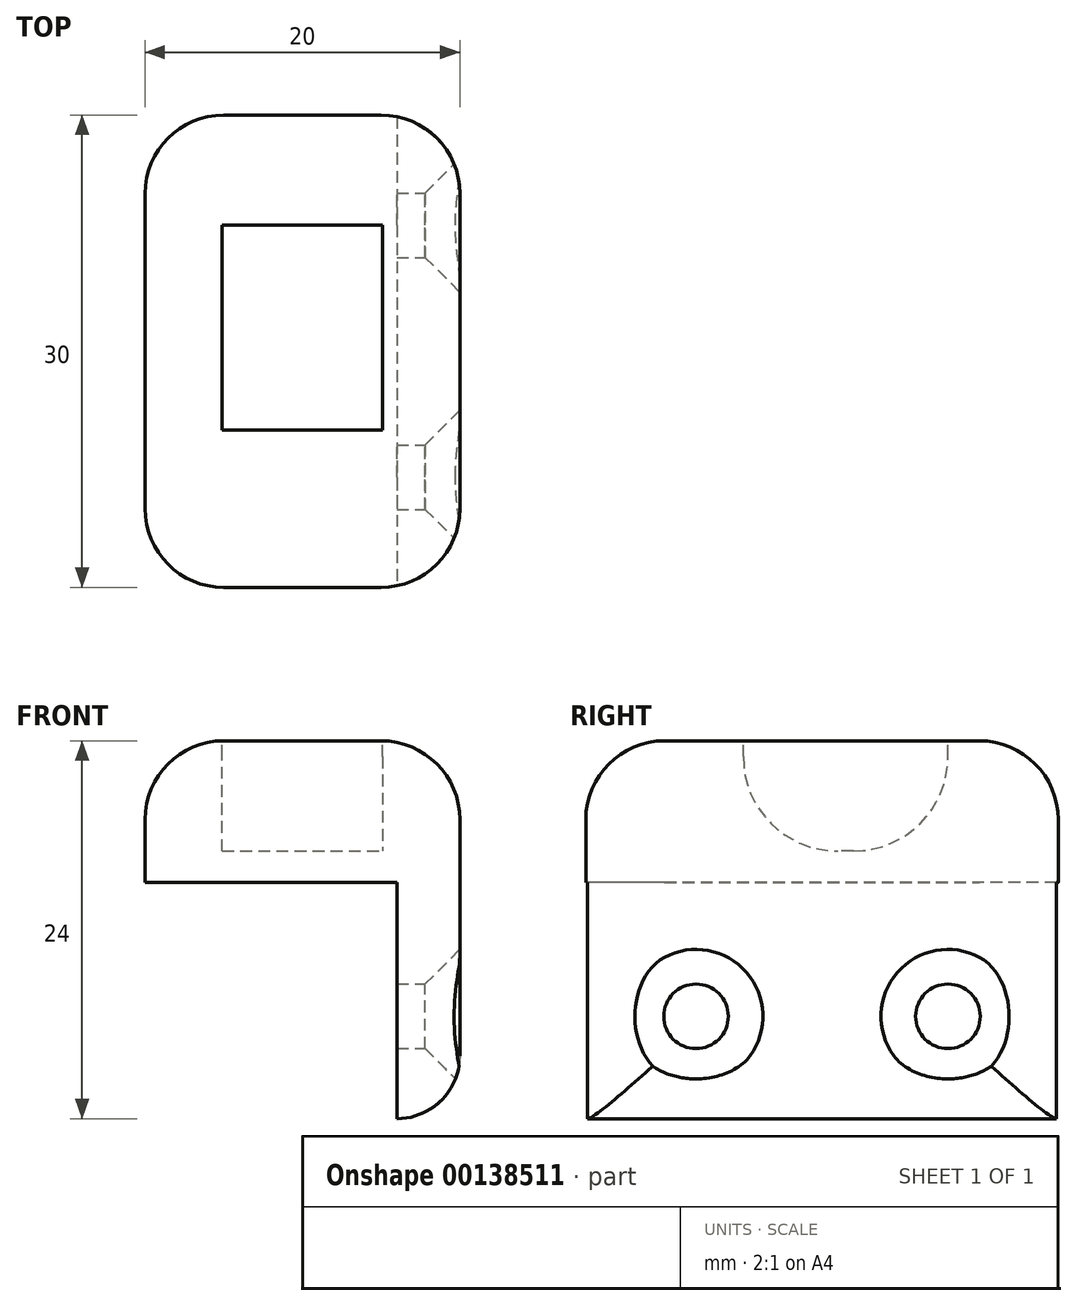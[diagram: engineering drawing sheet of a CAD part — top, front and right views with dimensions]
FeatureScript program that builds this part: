
annotation { "Feature Type Name" : "Feature", "Feature Type Description" : "" }
export const myFeature = defineFeature(function(context is Context, id is Id, definition is map)
    precondition{}
    {
        {
            var Q0;
            Q0=qCreatedBy(makeId("Top.planeOp"),FACE);
            var sketch = newSketch(context, id + "F0", { "sketchPlane" : qUnion([Q0])});
            skLineSegment(sketch, "E0.bottom", {"start": v(0, 0) * mm, "end": v(-20, 0) * mm});
            skLineSegment(sketch, "E0.top", {"start": v(0, 30) * mm, "end": v(-20, 30) * mm});
            skLineSegment(sketch, "E0.left", {"start": v(0, 0) * mm, "end": v(0, 30) * mm});
            skLineSegment(sketch, "E0.right", {"start": v(-20, 0) * mm, "end": v(-20, 30) * mm});
            skSolve(sketch);
        }
        {
            var Q0;
            Q0=qSketchRegion(id+"F0",true);
            extrude(context, id + "F1", {"entities" : qUnion([Q0]), "depth" : 9 * mm});
        }
        {
            var Q0;
            Q0=qCreatedBy(makeId("Top.planeOp"),FACE);
            var sketch = newSketch(context, id + "F2", { "sketchPlane" : qUnion([Q0])});
            skLineSegment(sketch, "E1.bottom", {"start": v(0, 30) * mm, "end": v(-4, 30) * mm});
            skLineSegment(sketch, "E1.top", {"start": v(0, 0) * mm, "end": v(-4, 0) * mm});
            skLineSegment(sketch, "E1.left", {"start": v(0, 30) * mm, "end": v(0, 0) * mm});
            skLineSegment(sketch, "E1.right", {"start": v(-4, 30) * mm, "end": v(-4, 0) * mm});
            skSolve(sketch);
        }
        {
            var Q0;
            Q0=makeQuery(id+"F1.opExtrude","CAP_FACE",FACE,{"disambiguationData":[OSD([sQuery(id+"F0.wireOp",EDGE,"E0.bottom"),sQuery(id+"F0.wireOp",EDGE,"E0.top"),sQuery(id+"F0.wireOp",EDGE,"E0.left"),sQuery(id+"F0.wireOp",EDGE,"E0.right")])],"isStart":false});
            cPlane(context, id + "F3", {"entities" : qUnion([Q0]), "cplaneType" : CPlaneType.OFFSET, "offset" : 0 * mm, "width" : 150 * mm, "height" : 150 * mm});
        }
        {
            var Q0;
            Q0=qCreatedBy(id+"F3.planeOp",FACE);
            var sketch = newSketch(context, id + "F4", { "sketchPlane" : qUnion([Q0])});
            skLineSegment(sketch, "E2.bottom", {"start": v(-15.1, 23) * mm, "end": v(-4.9, 23) * mm});
            skLineSegment(sketch, "E2.top", {"start": v(-15.1, 10) * mm, "end": v(-4.9, 10) * mm});
            skLineSegment(sketch, "E2.left", {"start": v(-15.1, 23) * mm, "end": v(-15.1, 10) * mm});
            skLineSegment(sketch, "E2.right", {"start": v(-4.9, 23) * mm, "end": v(-4.9, 10) * mm});
            skSolve(sketch);
        }
        {
            var Q0;
            Q0=qSketchRegion(id+"F4",true);
            extrude(context, id + "F5", {"entities" : qUnion([Q0]), "operationType" : NewBodyOperationType.REMOVE, "oppositeDirection" : true, "depth" : 7 * mm});
        }
        {
            var Q0;
            Q0 = qSketchRegion(id + "F2", true);
            extrude(context, id + "F6", {"entities" : qUnion([Q0]), "operationType" : NewBodyOperationType.ADD, "oppositeDirection" : true, "depth" : 15 * mm});
        }
        {
            var Q0;
            Q0=makeQuery(id+"F5.boolean.opBoolean","COPY",EDGE,{"derivedFrom":makeQuery(id+"F5.opExtrude","CAP_EDGE",EDGE,{"disambiguationData":[OSD([sQuery(id+"F4.wireOp",EDGE,"E2.top")])],"isStart":false})});
            var Q1;
            Q1=makeQuery(id+"F5.boolean.opBoolean","COPY",EDGE,{"derivedFrom":makeQuery(id+"F5.opExtrude","CAP_EDGE",EDGE,{"disambiguationData":[OSD([sQuery(id+"F4.wireOp",EDGE,"E2.bottom")])],"isStart":false})});
            fillet(context, id + "F7", {"entities" : qUnion([Q0, Q1]), "radius" : 6 * mm, "tangentPropagation" : true, "allowEdgeOverflow" : false});
        }
        {
            var Q0;
            Q0=makeQuery(id+"F6.boolean.opBoolean","MERGE",FACE,{"derivedFrom":[makeQuery(id+"F1.opExtrude","SWEPT_FACE",FACE,{"disambiguationData":[OSD([sQuery(id+"F0.wireOp",EDGE,"E0.left")])]}),makeQuery(id+"F6.opExtrude","SWEPT_FACE",FACE,{"disambiguationData":[OSD([sQuery(id+"F2.wireOp",EDGE,"E1.left")])]})]});
            cPlane(context, id + "F8", {"entities" : qUnion([Q0]), "cplaneType" : CPlaneType.OFFSET, "offset" : 0 * mm, "width" : 150 * mm, "height" : 150 * mm});
        }
        {
            var Q0;
            Q0=qCreatedBy(id+"F8.planeOp",FACE);
            var sketch = newSketch(context, id + "F9", { "sketchPlane" : qUnion([Q0])});
            skPoint(sketch, "E3", {"position": v(7, -8.5) * mm});
            skPoint(sketch, "E4", {"position": v(23, -8.5) * mm});
            skSolve(sketch);
        }
        {
            var Q0;
            Q0=sQuery(id+"F9.wireOp",VERTEX,"E3");
            var Q1;
            Q1=sQuery(id+"F9.wireOp",VERTEX,"E4");
            var Q2;
            Q2=makeQuery(id+"F1.opExtrude","SWEPT_BODY",BODY,{"disambiguationData":[OSD([sQuery(id+"F0.wireOp",EDGE,"E0.bottom"),sQuery(id+"F0.wireOp",EDGE,"E0.top"),sQuery(id+"F0.wireOp",EDGE,"E0.left"),sQuery(id+"F0.wireOp",EDGE,"E0.right")])]});
            hole(context, id + "F10", {"style" : HoleStyle.C_SINK, "endStyle" : HoleEndStyle.THROUGH, "holeDiameter" : 4.1 * mm, "cSinkDiameter" : 8.5 * mm, "cSinkAngle" : 90 * degree, "locations" : qUnion([Q0, Q1]), "scope" : qUnion([Q2]), "tappedDepth" : 12 * mm, "tapClearance" : 3});
        }
        {
            var Q0;
            Q0=makeQuery(id+"F1.opExtrude","CAP_EDGE",EDGE,{"disambiguationData":[OSD([sQuery(id+"F0.wireOp",EDGE,"E0.left")])],"isStart":false});
            var Q1;
            Q1=makeQuery(id+"F1.opExtrude","CAP_EDGE",EDGE,{"disambiguationData":[OSD([sQuery(id+"F0.wireOp",EDGE,"E0.right")])],"isStart":false});
            var Q2;
            Q2=makeQuery(id+"F1.opExtrude","CAP_EDGE",EDGE,{"disambiguationData":[OSD([sQuery(id+"F0.wireOp",EDGE,"E0.bottom")])],"isStart":false});
            var Q3;
            Q3=makeQuery(id+"F1.opExtrude","CAP_EDGE",EDGE,{"disambiguationData":[OSD([sQuery(id+"F0.wireOp",EDGE,"E0.top")])],"isStart":false});
            fillet(context, id + "F11", {"entities" : qUnion([Q0, Q1, Q2, Q3]), "radius" : 5 * mm, "tangentPropagation" : true, "allowEdgeOverflow" : false});
        }
        {
            var Q0;
            Q0=makeQuery(id+"F1.opExtrude","SWEPT_EDGE",EDGE,{"disambiguationData":[OSD([sQuery(id+"F0.wireOp",EDGE,"E0.bottom"),sQuery(id+"F0.wireOp",EDGE,"E0.right")])]});
            var Q1;
            Q1=makeQuery(id+"F1.opExtrude","SWEPT_EDGE",EDGE,{"disambiguationData":[OSD([sQuery(id+"F0.wireOp",EDGE,"E0.top"),sQuery(id+"F0.wireOp",EDGE,"E0.right")])]});
            var Q2;
            Q2=makeQuery(id+"F6.boolean.opBoolean","MERGE",EDGE,{"derivedFrom":[makeQuery(id+"F1.opExtrude","SWEPT_EDGE",EDGE,{"disambiguationData":[OSD([sQuery(id+"F0.wireOp",EDGE,"E0.bottom"),sQuery(id+"F0.wireOp",EDGE,"E0.left")])]}),makeQuery(id+"F6.opExtrude","SWEPT_EDGE",EDGE,{"disambiguationData":[OSD([sQuery(id+"F2.wireOp",EDGE,"E1.top"),sQuery(id+"F2.wireOp",EDGE,"E1.left")])]})]});
            var Q3;
            Q3=makeQuery(id+"F6.boolean.opBoolean","MERGE",EDGE,{"derivedFrom":[makeQuery(id+"F1.opExtrude","SWEPT_EDGE",EDGE,{"disambiguationData":[OSD([sQuery(id+"F0.wireOp",EDGE,"E0.top"),sQuery(id+"F0.wireOp",EDGE,"E0.left")])]}),makeQuery(id+"F6.opExtrude","SWEPT_EDGE",EDGE,{"disambiguationData":[OSD([sQuery(id+"F2.wireOp",EDGE,"E1.bottom"),sQuery(id+"F2.wireOp",EDGE,"E1.left")])]})]});
            fillet(context, id + "F12", {"entities" : qUnion([Q0, Q1, Q2, Q3]), "radius" : 5 * mm, "tangentPropagation" : true, "allowEdgeOverflow" : false});
        }
        {
            var Q0;
            Q0=makeQuery(id+"F6.opExtrude","CAP_EDGE",EDGE,{"disambiguationData":[OSD([sQuery(id+"F2.wireOp",EDGE,"E1.left")])],"isStart":false});
            fillet(context, id + "F13", {"entities" : qUnion([Q0]), "radius" : 4 * mm, "tangentPropagation" : true, "allowEdgeOverflow" : false});
        }
    });
